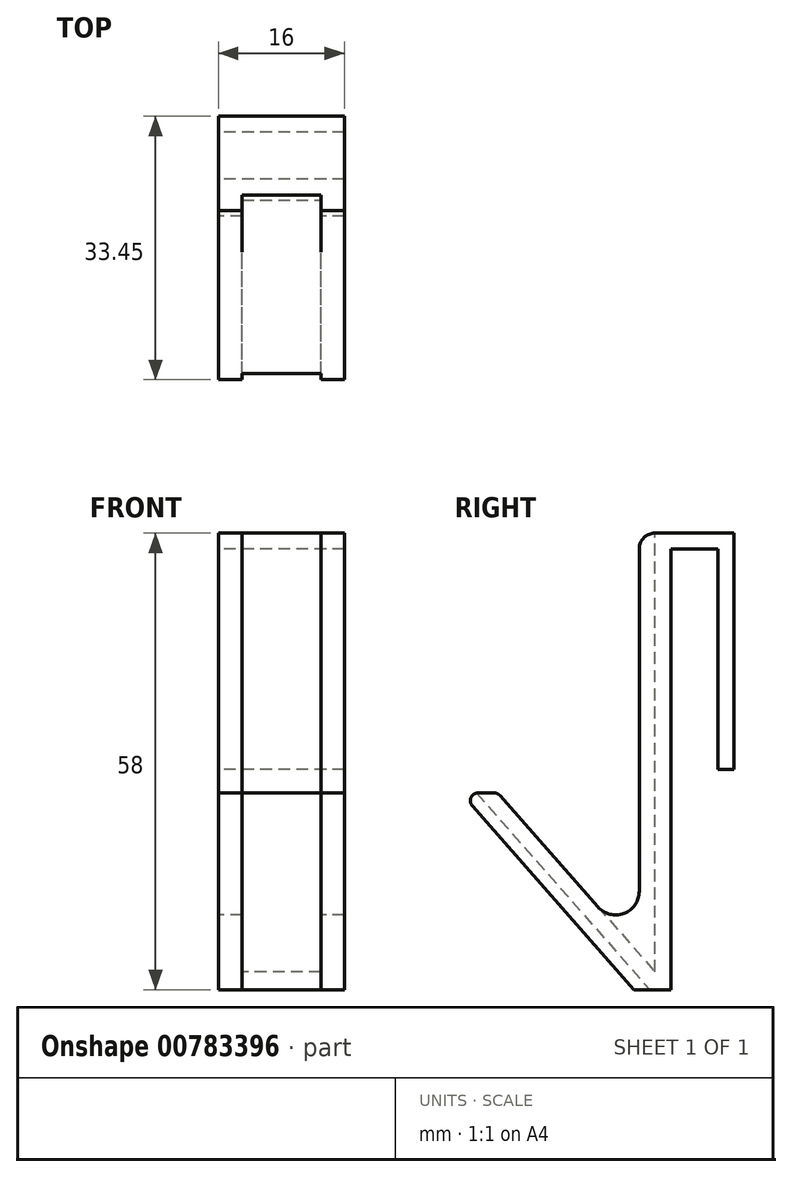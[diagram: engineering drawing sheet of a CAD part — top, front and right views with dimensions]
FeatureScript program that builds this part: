
annotation { "Feature Type Name" : "Feature", "Feature Type Description" : "" }
export const myFeature = defineFeature(function(context is Context, id is Id, definition is map)
    precondition{}
    {
        {
            var Q0;
            Q0=qCreatedBy(makeId("Right.planeOp"),FACE);
            var sketch = newSketch(context, id + "F0", { "sketchPlane" : qUnion([Q0])});
            skLineSegment(sketch, "E0", {"start": v(-61.8, -143.6) * mm, "end": v(-61.8, -87.88) * mm});
            skLineSegment(sketch, "E1", {"start": v(-61.8, -87.88) * mm, "end": v(-51.8, -87.88) * mm});
            skLineSegment(sketch, "E2", {"start": v(-51.8, -87.88) * mm, "end": v(-51.8, -117.88) * mm});
            skLineSegment(sketch, "E3", {"start": v(-51.8, -117.88) * mm, "end": v(-53.8, -117.88) * mm});
            skLineSegment(sketch, "E4", {"start": v(-53.8, -117.88) * mm, "end": v(-53.8, -89.88) * mm});
            skLineSegment(sketch, "E5", {"start": v(-53.8, -89.88) * mm, "end": v(-59.8, -89.88) * mm});
            skLineSegment(sketch, "E6", {"start": v(-59.8, -89.88) * mm, "end": v(-59.8, -145.88) * mm});
            skLineSegment(sketch, "E7", {"start": v(-61.8, -143.6) * mm, "end": v(-81.8, -120.88) * mm});
            skLineSegment(sketch, "E8", {"start": v(-86.46, -120.88) * mm, "end": v(-64.46, -145.88) * mm});
            skLineSegment(sketch, "E9", {"start": v(-64.46, -145.88) * mm, "end": v(-59.8, -145.88) * mm});
            skLineSegment(sketch, "E10", {"start": v(-86.46, -120.88) * mm, "end": v(-81.8, -120.88) * mm});
            skSolve(sketch);
        }
        {
            var Q0;
            Q0=makeQuery(id+"F0.imprint","IMPRINT",FACE,{"disambiguationData":[TD([[makeQuery(id+"F0.imprint","IMPRINT",EDGE,{"derivedFrom":sQuery(id+"F0.wireOp",EDGE,"E0")}),-1.0]])]});
            extrude(context, id + "F1", {"entities" : qUnion([Q0]), "depth" : 16 * mm, "offsetDistance" : 25 * mm});
        }
        {
            var Q0;
            Q0=makeQuery(id+"F1.opExtrude","SWEPT_FACE",FACE,{"disambiguationData":[OSD([sQuery(id+"F0.wireOp",EDGE,"E1")])]});
            var sketch = newSketch(context, id + "F2", { "sketchPlane" : qUnion([Q0])});
            skLineSegment(sketch, "E11.bottom", {"start": v(0, -61.8) * mm, "end": v(3, -61.8) * mm});
            skLineSegment(sketch, "E11.top", {"start": v(0, -63.8) * mm, "end": v(3, -63.8) * mm});
            skLineSegment(sketch, "E11.left", {"start": v(0, -61.8) * mm, "end": v(0, -63.8) * mm});
            skLineSegment(sketch, "E11.right", {"start": v(3, -61.8) * mm, "end": v(3, -63.8) * mm});
            skLineSegment(sketch, "E12.bottom", {"start": v(16, -61.8) * mm, "end": v(13, -61.8) * mm});
            skLineSegment(sketch, "E12.top", {"start": v(16, -63.8) * mm, "end": v(13, -63.8) * mm});
            skLineSegment(sketch, "E12.left", {"start": v(16, -61.8) * mm, "end": v(16, -63.8) * mm});
            skLineSegment(sketch, "E12.right", {"start": v(13, -61.8) * mm, "end": v(13, -63.8) * mm});
            skSolve(sketch);
        }
        {
            var Q0;
            Q0=makeQuery(id+"F2.imprint","IMPRINT",FACE,{"disambiguationData":[TD([[makeQuery(id+"F2.imprint","IMPRINT",EDGE,{"derivedFrom":sQuery(id+"F2.wireOp",EDGE,"E11.bottom")}),1.0]])]});
            var Q1;
            Q1=makeQuery(id+"F2.imprint","IMPRINT",FACE,{"disambiguationData":[TD([[makeQuery(id+"F2.imprint","IMPRINT",EDGE,{"derivedFrom":sQuery(id+"F2.wireOp",EDGE,"E12.bottom")}),1.0]])]});
            extrude(context, id + "F3", {"entities" : qUnion([Q0, Q1]), "operationType" : NewBodyOperationType.ADD, "oppositeDirection" : true, "depth" : 58 * mm, "offsetDistance" : 25 * mm});
        }
        {
            var Q0;
            Q0=makeQuery(id+"F1.opExtrude","SWEPT_FACE",FACE,{"disambiguationData":[OSD([sQuery(id+"F0.wireOp",EDGE,"E10")])]});
            var sketch = newSketch(context, id + "F4", { "sketchPlane" : qUnion([Q0])});
            skLineSegment(sketch, "E13.bottom", {"start": v(3, -86.46) * mm, "end": v(13, -86.46) * mm});
            skLineSegment(sketch, "E13.top", {"start": v(3, -84.46) * mm, "end": v(13, -84.46) * mm});
            skLineSegment(sketch, "E13.left", {"start": v(3, -86.46) * mm, "end": v(3, -84.46) * mm});
            skLineSegment(sketch, "E13.right", {"start": v(13, -86.46) * mm, "end": v(13, -84.46) * mm});
            skSolve(sketch);
        }
        {
            var Q0;
            Q0=makeQuery(id+"F4.imprint","IMPRINT",FACE,{"disambiguationData":[TD([[makeQuery(id+"F4.imprint","IMPRINT",EDGE,{"derivedFrom":sQuery(id+"F4.wireOp",EDGE,"E13.bottom")}),-1.0]])]});
            var Q1;
            Q1=makeQuery(id+"F1.opExtrude","CAP_EDGE",EDGE,{"disambiguationData":[OSD([sQuery(id+"F0.wireOp",EDGE,"E8")])],"isStart":false});
            sweep(context, id + "F5", {"operationType" : NewBodyOperationType.REMOVE, "profiles" : qUnion([Q0]), "path" : qUnion([Q1])});
        }
        {
            var Q0;
            {var subQ0=sQuery(id+"F0.wireOp",EDGE,"E10");var subQ1=sQuery(id+"F0.wireOp",EDGE,"E8");Q0=makeQuery(id+"F5.boolean.opBoolean","SPLIT",EDGE,{"disambiguationData":[TD([makeQuery(id+"F3.opExtrude","SWEPT_FACE",FACE,{"disambiguationData":[OSD([sQuery(id+"F2.wireOp",EDGE,"E11.left")])]})])],"derivedFrom":makeQuery(id+"F1.opExtrude","SWEPT_EDGE",EDGE,{"disambiguationData":[OSD([subQ1,subQ0])]})});}
            var Q1;
            {var subQ0=sQuery(id+"F0.wireOp",EDGE,"E8");var subQ1=sQuery(id+"F0.wireOp",EDGE,"E10");Q1=makeQuery(id+"F5.boolean.opBoolean","SPLIT",EDGE,{"disambiguationData":[TD([makeQuery(id+"F3.opExtrude","SWEPT_FACE",FACE,{"disambiguationData":[OSD([sQuery(id+"F2.wireOp",EDGE,"E12.left")])]})])],"derivedFrom":makeQuery(id+"F1.opExtrude","SWEPT_EDGE",EDGE,{"disambiguationData":[OSD([subQ0,subQ1])]})});}
            fillet(context, id + "F6", {"entities" : qUnion([Q0, Q1]), "radius" : 1 * mm, "tangentPropagation" : true, "allowEdgeOverflow" : false});
        }
        {
            var Q0;
            Q0=makeQuery(id+"F1.opExtrude","SWEPT_EDGE",EDGE,{"disambiguationData":[OSD([sQuery(id+"F0.wireOp",EDGE,"E7"),sQuery(id+"F0.wireOp",EDGE,"E10")])]});
            fillet(context, id + "F7", {"entities" : qUnion([Q0]), "radius" : 1 * mm, "tangentPropagation" : true, "allowEdgeOverflow" : false});
        }
        {
            var Q0;
            Q0=makeQuery(id+"F3.opExtrude","CAP_EDGE",EDGE,{"disambiguationData":[OSD([sQuery(id+"F2.wireOp",EDGE,"E12.top")])],"isStart":true});
            var Q1;
            Q1=makeQuery(id+"F3.opExtrude","CAP_EDGE",EDGE,{"disambiguationData":[OSD([sQuery(id+"F2.wireOp",EDGE,"E11.top")])],"isStart":true});
            fillet(context, id + "F8", {"entities" : qUnion([Q0, Q1]), "radius" : 2 * mm, "tangentPropagation" : true, "allowEdgeOverflow" : false});
        }
        {
            var Q0;
            Q0=makeQuery(id+"F3.boolean.opBoolean","INTERSECT",EDGE,{"derivedFrom":[makeQuery(id+"F1.opExtrude","SWEPT_FACE",FACE,{"disambiguationData":[OSD([sQuery(id+"F0.wireOp",EDGE,"E7")])]}),makeQuery(id+"F3.opExtrude","SWEPT_FACE",FACE,{"disambiguationData":[OSD([sQuery(id+"F2.wireOp",EDGE,"E12.top")])]})]});
            var Q1;
            Q1=makeQuery(id+"F3.boolean.opBoolean","INTERSECT",EDGE,{"derivedFrom":[makeQuery(id+"F1.opExtrude","SWEPT_FACE",FACE,{"disambiguationData":[OSD([sQuery(id+"F0.wireOp",EDGE,"E7")])]}),makeQuery(id+"F3.opExtrude","SWEPT_FACE",FACE,{"disambiguationData":[OSD([sQuery(id+"F2.wireOp",EDGE,"E11.top")])]})]});
            fillet(context, id + "F9", {"entities" : qUnion([Q0, Q1]), "radius" : 3 * mm, "tangentPropagation" : true, "allowEdgeOverflow" : false});
        }
    });
